# Revit family: Access_Controller-Vicon-VAX-Control_Box
name_source: partatom
category: Security Devices
revit_build: Autodesk Revit 2014 (Build: 20140709_2115(x64)
units: mm (PartAtom-declared; Revit-internal decimal feet)

## types (4) — shared parameters
Apparent Load = 20 VA
Assembly Code = E1010110
Connector Description = Connector for Electrical Power
Connector Type = 802.3af PoE/PoE+
Default Elevation = 48"
Depth = 2 1/2"
Height = 3 1/2"
Housing Material = Metal - Vicon - Cast Aluminum - Black
Load Classification = Power
Manufacturer = Vicon Industries
Number of Poles = 1
Operating Temperature = 32 to 122 Degrees Fahrenheit
Power Factor = 1
Product Documentation Link = http://www.vicon-security.com
Product Page URL = http://www.vicon-security.com
URL = http://www.vicon-security.com
Voltage = 12 V
Voltage Range = PoE, 12-24VDC
Watts = 20 W
Weight = 0.90 lb
Width = 10"

## per-type parameters (varying)
| type | Description | Operating Humidity |
| VAX-1D-REX | Vicon Single Door Access Control Box with integrated PIR/REX | 10% to 90% relative, non-condensing |
| VAX-2D | Vicon Two Door Access Control Box without integrated PIR/REX | 10% to 90% relative humidity, non-condensing |
| VAX-2D-REX | Vicon Two Door Access Control Box with integrated PIR/REX | 10% to 90% relative, non-condensing |
| VAX-1D | Vicon Single Door Access Control Box without integrated PIR/REX | 10% to 90% relative, non-condensing |

note: column(s) folded — value = type name in every type: Model

## geometry (parser evidence)
native form markers: Sweep x5
no freeform markers — native parametric forms only
